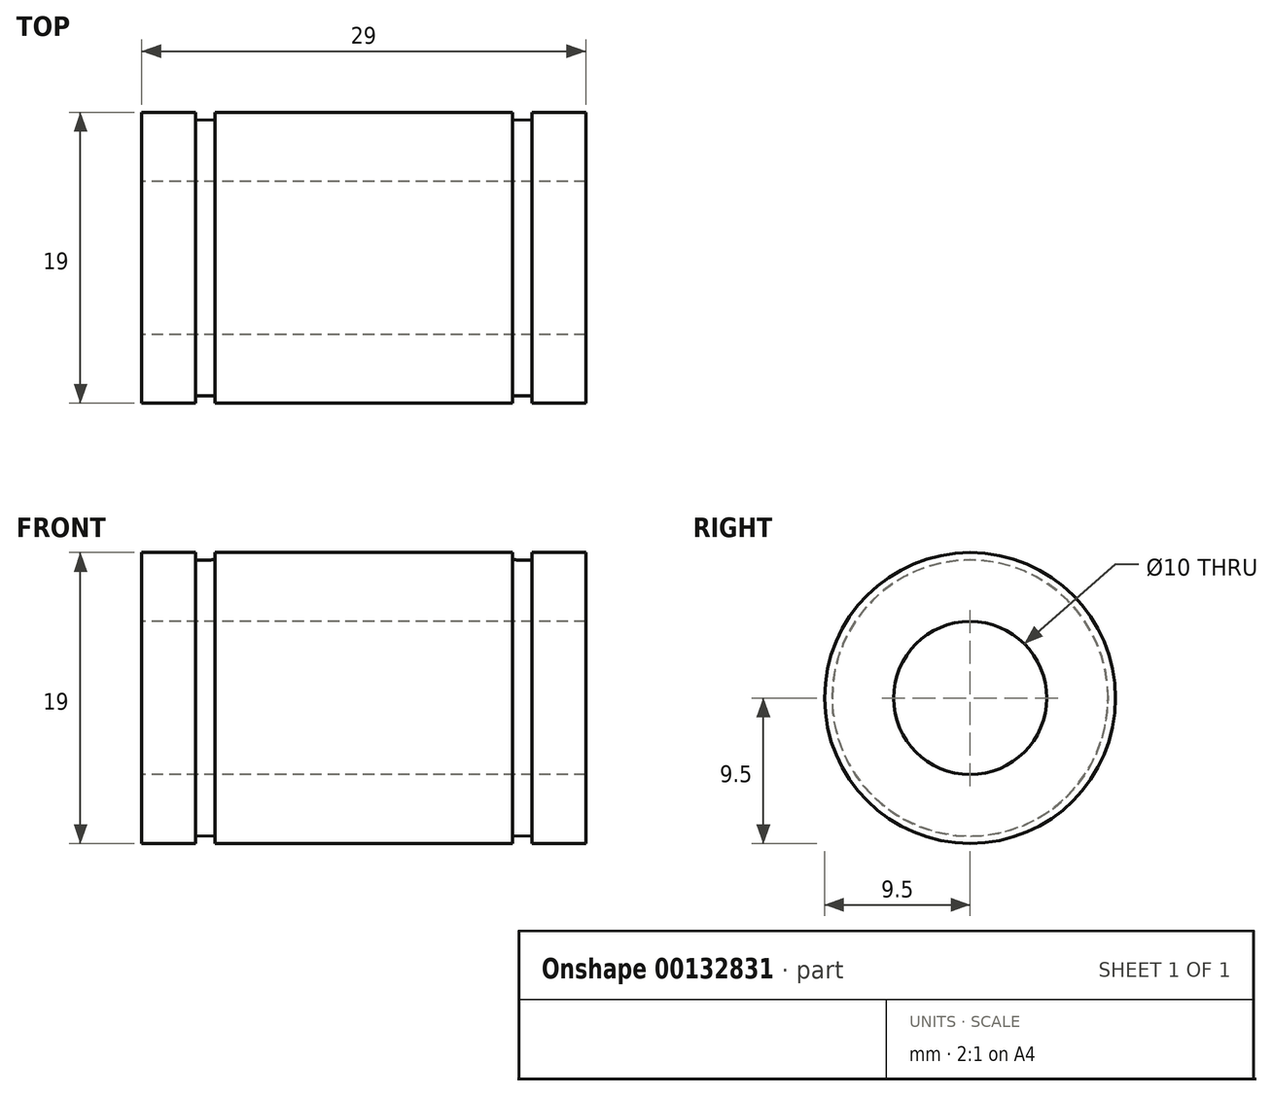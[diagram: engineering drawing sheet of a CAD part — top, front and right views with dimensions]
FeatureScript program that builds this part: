
annotation { "Feature Type Name" : "Feature", "Feature Type Description" : "" }
export const myFeature = defineFeature(function(context is Context, id is Id, definition is map)
    precondition{}
    {
        {
            var Q0;
            Q0=qCreatedBy(makeId("Front.planeOp"),FACE);
            var sketch = newSketch(context, id + "F0", { "sketchPlane" : qUnion([Q0])});
            skLineSegment(sketch, "E0.bottom", {"start": v(-14.5, 0) * mm, "end": v(14.5, 0) * mm});
            skLineSegment(sketch, "E0.top", {"start": v(-14.5, 9.5) * mm, "end": v(14.5, 9.5) * mm});
            skLineSegment(sketch, "E0.left", {"start": v(-14.5, 0) * mm, "end": v(-14.5, 9.5) * mm});
            skLineSegment(sketch, "E0.right", {"start": v(14.5, 0) * mm, "end": v(14.5, 9.5) * mm});
            skLineSegment(sketch, "E1", {"start": v(-14.5, 5) * mm, "end": v(14.5, 5) * mm});
            skLineSegment(sketch, "E2", {"start": v(-14.5, 9) * mm, "end": v(14.5, 9) * mm, "construction": true});
            skLineSegment(sketch, "E3", {"start": v(-11, 9.5) * mm, "end": v(-11, 9) * mm});
            skLineSegment(sketch, "E4", {"start": v(-9.7, 9.5) * mm, "end": v(-9.7, 9) * mm});
            skLineSegment(sketch, "E5.MirrorCS", {"start": v(9.7, 9.5) * mm, "end": v(9.7, 9) * mm});
            skLineSegment(sketch, "E6.MirrorCS", {"start": v(11, 9.5) * mm, "end": v(11, 9) * mm});
            skLineSegment(sketch, "E7", {"start": v(-11, 9) * mm, "end": v(-9.7, 9.03) * mm});
            skLineSegment(sketch, "E8.MirrorCS", {"start": v(11, 9) * mm, "end": v(9.7, 9.03) * mm});
            skSolve(sketch);
        }
        {
            var Q0;
            {var subQ11=sQuery(id+"F0.wireOp",EDGE,"E1");Q0=makeQuery(id+"F0.imprint","IMPRINT",FACE,{"disambiguationData":[TD([[makeQuery(id+"F0.imprint","IMPRINT",EDGE,{"derivedFrom":subQ11}),1.0]])]});}
            var Q1;
            Q1=sQuery(id+"F0.wireOp",EDGE,"E0.bottom");
            revolve(context, id + "F1", {"entities" : qUnion([Q0]), "axis" : qUnion([Q1]), "revolveType" : RevolveType.FULL});
        }
    });
